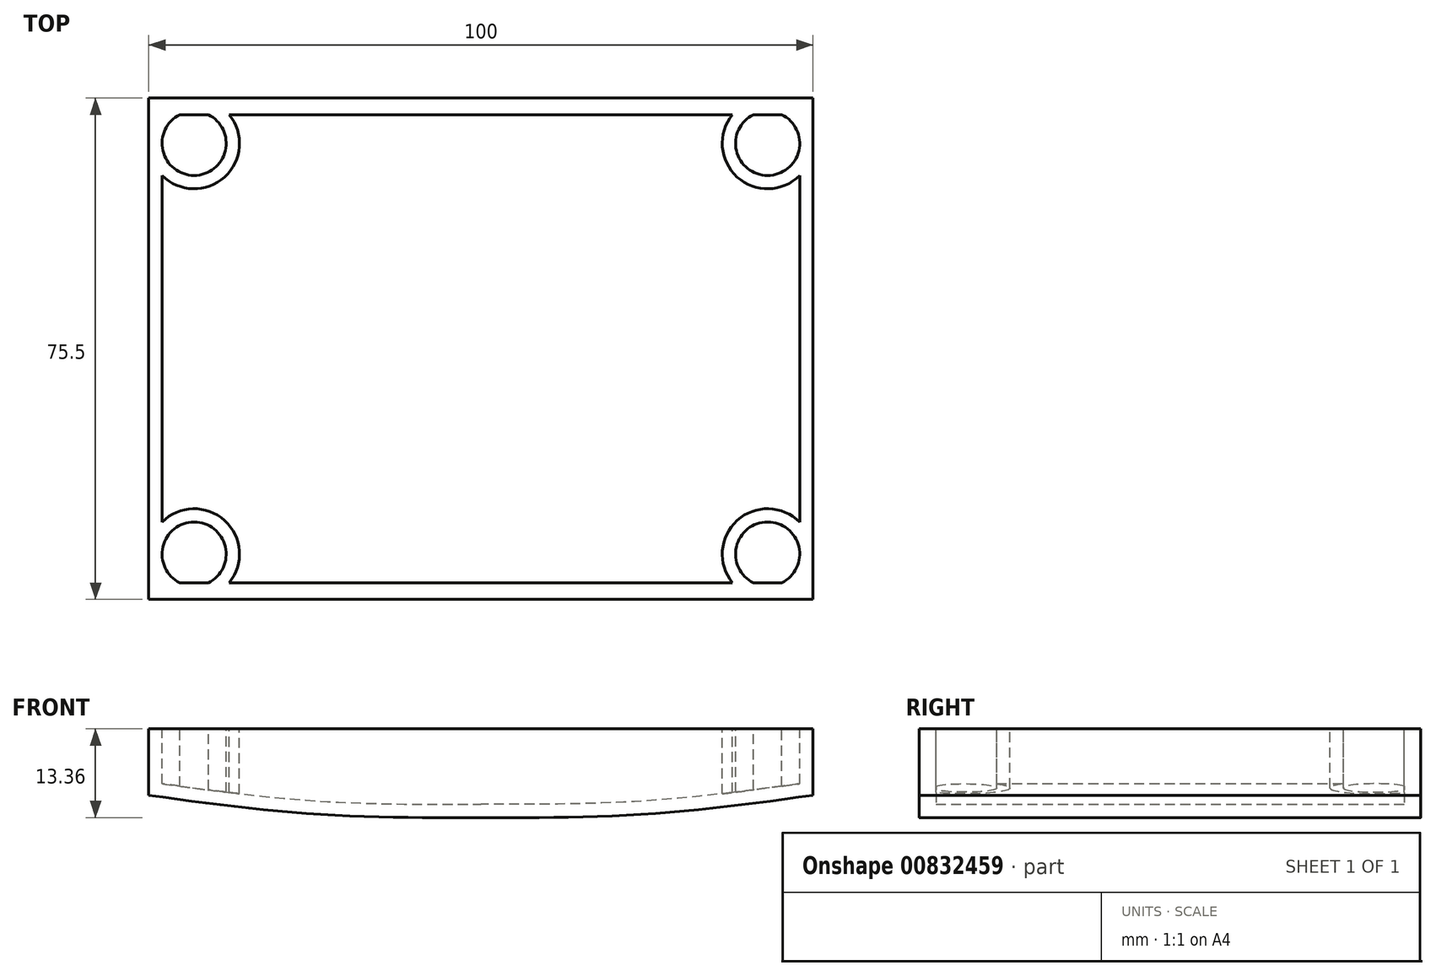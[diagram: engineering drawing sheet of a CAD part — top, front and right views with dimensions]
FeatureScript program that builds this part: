
annotation { "Feature Type Name" : "Feature", "Feature Type Description" : "" }
export const myFeature = defineFeature(function(context is Context, id is Id, definition is map)
    precondition{}
    {
        {
            var Q0;
            Q0=qCreatedBy(makeId("Front.planeOp"),FACE);
            var sketch = newSketch(context, id + "F0", { "sketchPlane" : qUnion([Q0])});
            skLineSegment(sketch, "E0.top", {"start": v(0, 10) * mm, "end": v(-50, 10) * mm});
            skLineSegment(sketch, "E0.right", {"start": v(-50, 0) * mm, "end": v(-50, 10) * mm});
            skLineSegment(sketch, "E1.MirrorCS", {"start": v(0, 10) * mm, "end": v(50, 10) * mm});
            skLineSegment(sketch, "E2.MirrorCS", {"start": v(50, 0) * mm, "end": v(50, 10) * mm});
            skFitSpline(sketch, "E3", {"points": [v(-50, 0) * mm, v(-25.31, -2.81) * mm, v(0, -3.36) * mm], "startDerivative": vector(49.41, -6.79) * mm, "endDerivative": vector(50.58, 0.06) * mm});
            skFitSpline(sketch, "E4.MirrorCS", {"points": [v(50, 0) * mm, v(25.31, -2.81) * mm, v(0, -3.36) * mm], "startDerivative": vector(-49.41, -6.79) * mm, "endDerivative": vector(-50.58, 0.06) * mm});
            skSolve(sketch);
        }
        {
            var Q0;
            Q0=makeQuery(id+"F0.imprint","IMPRINT",FACE,{"disambiguationData":[TD([[makeQuery(id+"F0.imprint","IMPRINT",EDGE,{"derivedFrom":sQuery(id+"F0.wireOp",EDGE,"E0.top")}),1.0]])]});
            extrude(context, id + "F1", {"entities" : qUnion([Q0]), "depth" : 75 * mm, "offsetDistance" : 25 * mm});
        }
        {
            var Q0;
            Q0=makeQuery(id+"F1.opExtrude","SWEPT_FACE",FACE,{"disambiguationData":[OSD([sQuery(id+"F0.wireOp",EDGE,"E0.top"),sQuery(id+"F0.wireOp",EDGE,"E1.MirrorCS")])]});
            shell(context, id + "F2", {"entities" : qUnion([Q0]), "thickness" : 2 * mm});
        }
        {
            var Q0;
            Q0=makeQuery(id+"F1.opExtrude","SWEPT_FACE",FACE,{"disambiguationData":[OSD([sQuery(id+"F0.wireOp",EDGE,"E0.top"),sQuery(id+"F0.wireOp",EDGE,"E1.MirrorCS")])]});
            var sketch = newSketch(context, id + "F3", { "sketchPlane" : qUnion([Q0])});
            skCircle(sketch, "E5", {"center": v(-43.17, -68.17) * mm, "radius": 4.83 * mm});
            skCircle(sketch, "E6", {"center": v(-43.17, -68.17) * mm, "radius": 6.83 * mm});
            skCircle(sketch, "E7.MirrorC", {"center": v(43.17, -68.17) * mm, "radius": 6.83 * mm});
            skCircle(sketch, "E8.MirrorC", {"center": v(43.17, -68.17) * mm, "radius": 4.83 * mm});
            skCircle(sketch, "E9.MirrorC", {"center": v(-45.73, -4.08) * mm, "radius": 1.98 * mm});
            skCircle(sketch, "E10.MirrorC", {"center": v(-45.73, -4.08) * mm, "radius": 3.08 * mm});
            skCircle(sketch, "E11.MirrorC", {"center": v(45.73, -4.08) * mm, "radius": 1.98 * mm});
            skCircle(sketch, "E12.MirrorC", {"center": v(45.73, -4.08) * mm, "radius": 3.08 * mm});
            skPoint(sketch, "E13.start.orphan", {"position": v(0, -37.5) * mm});
            skPoint(sketch, "E14.orphan", {"position": v(0, 0) * mm});
            skPoint(sketch, "E15.end.orphan", {"position": v(0, -75) * mm});
            skSolve(sketch);
        }
        {
            var Q0;
            {var subQ0=sQuery(id+"F3.wireOp",EDGE,"E5");var subQ1=sQuery(id+"F0.wireOp",EDGE,"E0.top");var subQ2=makeQuery(id+"F2.opShell","OFFSET_EDGE",EDGE,{"disambiguationData":[OSD([subQ1,sQuery(id+"F0.wireOp",EDGE,"E0.right")])]});var subQ3=makeQuery(id+"F3.imprint","INTERSECT",VERTEX,{"derivedFrom":[subQ2,subQ0]});Q0=makeQuery(id+"F3.imprint","IMPRINT",FACE,{"disambiguationData":[TD([[makeQuery(id+"F3.imprint","IMPRINT",EDGE,{"disambiguationData":[TD([[subQ3,1.0]])],"derivedFrom":subQ0}),-1.0]])]});}
            var Q1;
            {var subQ0=sQuery(id+"F3.wireOp",EDGE,"E5");var subQ1=sQuery(id+"F0.wireOp",EDGE,"E0.top");var subQ2=makeQuery(id+"F2.opShell","OFFSET_EDGE",EDGE,{"disambiguationData":[OSD([subQ1,sQuery(id+"F0.wireOp",EDGE,"E0.right")])]});var subQ3=makeQuery(id+"F3.imprint","INTERSECT",VERTEX,{"derivedFrom":[subQ2,subQ0]});Q1=makeQuery(id+"F3.imprint","IMPRINT",FACE,{"disambiguationData":[TD([[makeQuery(id+"F3.imprint","IMPRINT",EDGE,{"disambiguationData":[TD([[subQ3,-1.0]])],"derivedFrom":subQ0}),-1.0]])]});}
            extrude(context, id + "F4", {"entities" : qUnion([Q0, Q1]), "operationType" : NewBodyOperationType.ADD, "endBound" : BoundingType.UP_TO_NEXT, "oppositeDirection" : true, "depth" : 5 * mm, "offsetDistance" : 25 * mm});
        }
        {
            var Q0;
            Q0=makeQuery(id+"F1.opExtrude","SWEPT_BODY",BODY,{"disambiguationData":[OSD([sQuery(id+"F0.wireOp",EDGE,"E0.top"),sQuery(id+"F0.wireOp",EDGE,"E0.right"),sQuery(id+"F0.wireOp",EDGE,"E1.MirrorCS"),sQuery(id+"F0.wireOp",EDGE,"E2.MirrorCS"),sQuery(id+"F0.wireOp",EDGE,"E3"),sQuery(id+"F0.wireOp",EDGE,"E4.MirrorCS")])]});
            var Q1;
            Q1=qCreatedBy(makeId("Right.planeOp"),FACE);
            mirror(context, id + "F5", {"operationType" : NewBodyOperationType.ADD, "entities" : qUnion([Q0]), "mirrorPlane" : qUnion([Q1])});
        }
        {
            var Q0;
            Q0=qCreatedBy(makeId("Front.planeOp"),FACE);
            cPlane(context, id + "F6", {"entities" : qUnion([Q0]), "cplaneType" : CPlaneType.OFFSET, "offset" : 37.25 * mm, "width" : 150 * mm, "height" : 150 * mm});
        }
        {
            var Q0;
            Q0=makeQuery(id+"F1.opExtrude","SWEPT_BODY",BODY,{"disambiguationData":[OSD([sQuery(id+"F0.wireOp",EDGE,"E0.top"),sQuery(id+"F0.wireOp",EDGE,"E0.right"),sQuery(id+"F0.wireOp",EDGE,"E1.MirrorCS"),sQuery(id+"F0.wireOp",EDGE,"E2.MirrorCS"),sQuery(id+"F0.wireOp",EDGE,"E3"),sQuery(id+"F0.wireOp",EDGE,"E4.MirrorCS")])]});
            var Q1;
            Q1=qCreatedBy(id+"F6.planeOp",FACE);
            mirror(context, id + "F7", {"operationType" : NewBodyOperationType.ADD, "entities" : qUnion([Q0]), "mirrorPlane" : qUnion([Q1])});
        }
    });
